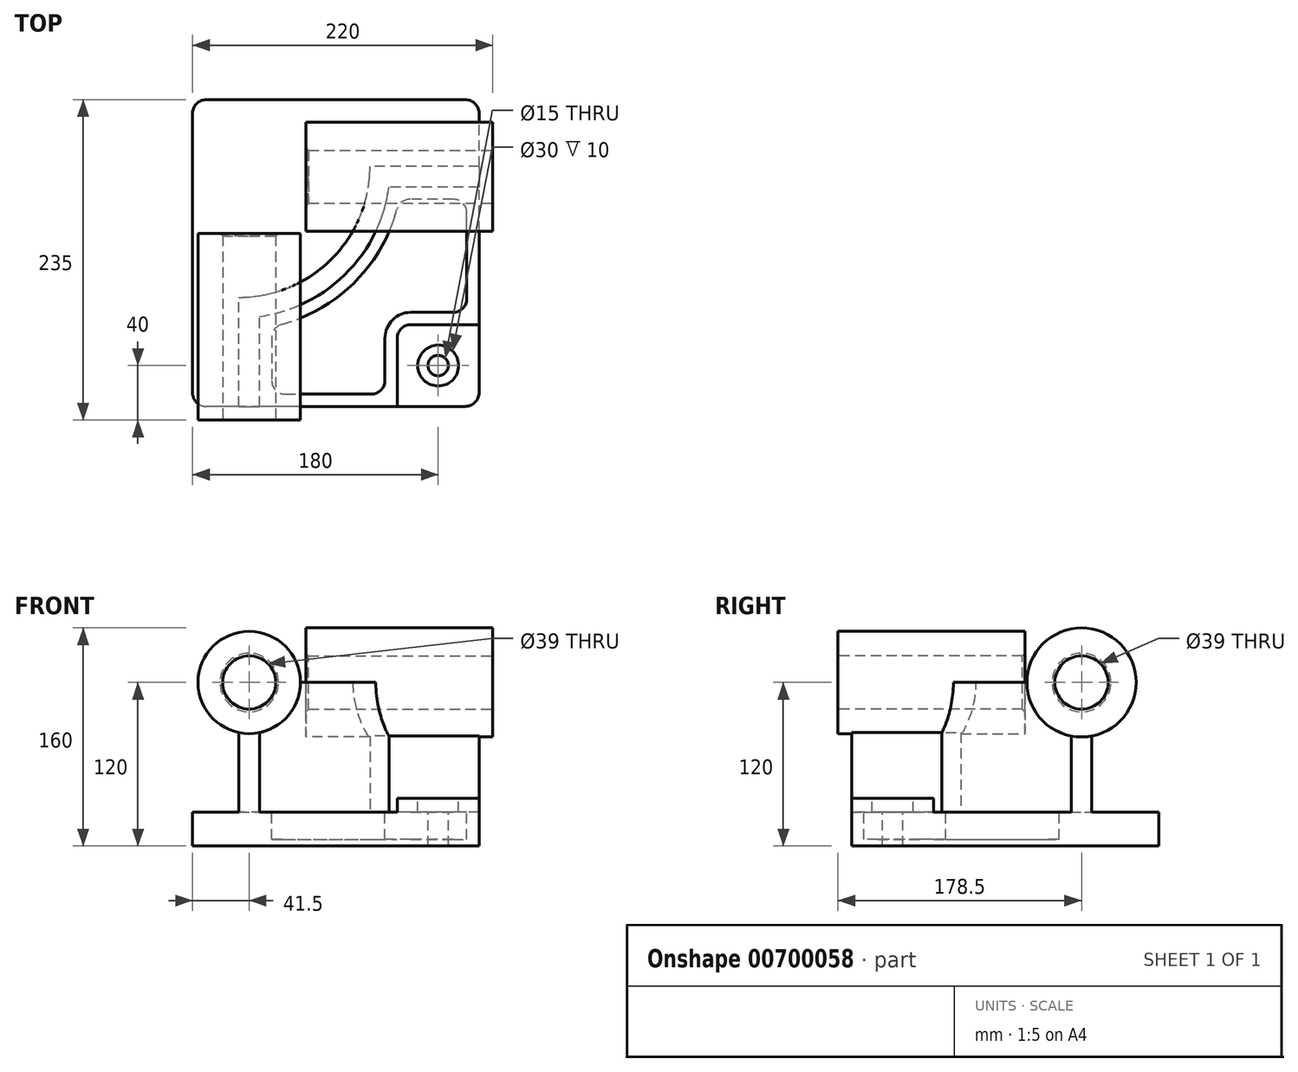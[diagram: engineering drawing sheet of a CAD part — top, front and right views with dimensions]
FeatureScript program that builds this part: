
annotation { "Feature Type Name" : "Feature", "Feature Type Description" : "" }
export const myFeature = defineFeature(function(context is Context, id is Id, definition is map)
    precondition{}
    {
        {
            var Q0;
            Q0=qCreatedBy(makeId("Top.planeOp"),FACE);
            var sketch = newSketch(context, id + "F0", { "sketchPlane" : qUnion([Q0])});
            skLineSegment(sketch, "E0.bottom", {"start": v(105, -112.5) * mm, "end": v(-105, -112.5) * mm});
            skLineSegment(sketch, "E0.top", {"start": v(105, 112.5) * mm, "end": v(-105, 112.5) * mm});
            skLineSegment(sketch, "E0.left", {"start": v(105, -112.5) * mm, "end": v(105, 112.5) * mm});
            skLineSegment(sketch, "E0.right", {"start": v(-105, -112.5) * mm, "end": v(-105, 112.5) * mm});
            skPoint(sketch, "E0.middle", {"position": v(0, 0) * mm});
            skSolve(sketch);
        }
        {
            var Q0;
            Q0=makeQuery(id+"F0.imprint","IMPRINT",FACE,{"disambiguationData":[TD([[makeQuery(id+"F0.imprint","IMPRINT",EDGE,{"derivedFrom":sQuery(id+"F0.wireOp",EDGE,"E0.bottom")}),-1.0]])]});
            extrude(context, id + "F1", {"entities" : qUnion([Q0]), "depth" : 25 * mm, "offsetDistance" : 25 * mm});
        }
        {
            var Q0;
            Q0=makeQuery(id+"F1.opExtrude","CAP_FACE",FACE,{"disambiguationData":[OSD([sQuery(id+"F0.wireOp",EDGE,"E0.bottom"),sQuery(id+"F0.wireOp",EDGE,"E0.top"),sQuery(id+"F0.wireOp",EDGE,"E0.left"),sQuery(id+"F0.wireOp",EDGE,"E0.right")])],"isStart":false});
            var sketch = newSketch(context, id + "F2", { "sketchPlane" : qUnion([Q0])});
            skLineSegment(sketch, "E1", {"start": v(-71, -112.5) * mm, "end": v(-71, -32.5) * mm});
            skLineSegment(sketch, "E2", {"start": v(105, 63.5) * mm, "end": v(25, 63.5) * mm});
            skArc(sketch, "E3", {"start": v(-71, -32.5) * mm, "mid": v(-3.12, -4.38) * mm, "end": v(25, 63.5) * mm});
            skLineSegment(sketch, "E4", {"start": v(-71, 63.5) * mm, "end": v(25, 63.5) * mm, "construction": true});
            skLineSegment(sketch, "E5", {"start": v(-71, 63.5) * mm, "end": v(-71, -32.5) * mm, "construction": true});
            skLineSegment(sketch, "E6.0", {"start": v(-56, -112.5) * mm, "end": v(-56, -46.48) * mm});
            skArc(sketch, "E6.1", {"start": v(-56, -46.48) * mm, "mid": v(7.49, -14.99) * mm, "end": v(38.98, 48.5) * mm});
            skLineSegment(sketch, "E6.2", {"start": v(105, 48.5) * mm, "end": v(38.98, 48.5) * mm});
            skLineSegment(sketch, "E7.0", {"start": v(105, -112.5) * mm, "end": v(105, 112.5) * mm});
            skLineSegment(sketch, "E8.0", {"start": v(105, -112.5) * mm, "end": v(-105, -112.5) * mm});
            skSolve(sketch);
        }
        {
            var Q0;
            {var subQ2=sQuery(id+"F2.wireOp",EDGE,"E1");Q0=makeQuery(id+"F2.imprint","IMPRINT",FACE,{"disambiguationData":[TD([[makeQuery(id+"F2.imprint","IMPRINT",EDGE,{"derivedFrom":subQ2}),-1.0]])]});}
            extrude(context, id + "F3", {"entities" : qUnion([Q0]), "operationType" : NewBodyOperationType.ADD, "depth" : 95 * mm, "offsetDistance" : 25 * mm});
        }
        {
            var Q0;
            Q0=makeQuery(id+"F3.boolean.opBoolean","MERGE",FACE,{"derivedFrom":[makeQuery(id+"F1.opExtrude","SWEPT_FACE",FACE,{"disambiguationData":[OSD([sQuery(id+"F0.wireOp",EDGE,"E0.bottom")])]}),makeQuery(id+"F3.opExtrude","SWEPT_FACE",FACE,{"disambiguationData":[OSD([sQuery(id+"F2.wireOp",EDGE,"E8.0")])]})]});
            var sketch = newSketch(context, id + "F4", { "sketchPlane" : qUnion([Q0])});
            skCircle(sketch, "E9", {"center": v(-63.5, 120) * mm, "radius": 37.5 * mm});
            skSolve(sketch);
        }
        {
            var Q0;
            Q0 = qSketchRegion(id + "F4", true);
            extrude(context, id + "F5", {"entities" : qUnion([Q0]), "operationType" : NewBodyOperationType.ADD, "depth" : 10 * mm, "offsetDistance" : 25 * mm, "hasSecondDirection" : true, "secondDirectionOppositeDirection" : true, "secondDirectionDepth" : (137 - 10) * mm});
        }
        {
            var Q0;
            Q0=makeQuery(id+"F3.boolean.opBoolean","MERGE",FACE,{"derivedFrom":[makeQuery(id+"F1.opExtrude","SWEPT_FACE",FACE,{"disambiguationData":[OSD([sQuery(id+"F0.wireOp",EDGE,"E0.left")])]}),makeQuery(id+"F3.opExtrude","SWEPT_FACE",FACE,{"disambiguationData":[OSD([sQuery(id+"F2.wireOp",EDGE,"E7.0")])]})]});
            var sketch = newSketch(context, id + "F6", { "sketchPlane" : qUnion([Q0])});
            skCircle(sketch, "E10", {"center": v(56, 120) * mm, "radius": 40 * mm});
            skSolve(sketch);
        }
        {
            var Q0;
            Q0 = qSketchRegion(id + "F6", true);
            extrude(context, id + "F7", {"entities" : qUnion([Q0]), "operationType" : NewBodyOperationType.ADD, "depth" : 10 * mm, "offsetDistance" : 25 * mm, "hasSecondDirection" : true, "secondDirectionOppositeDirection" : true, "secondDirectionDepth" : (137 - 10) * mm});
        }
        {
            var Q0;
            {var subQ0=sQuery(id+"F0.wireOp",EDGE,"E0.left");var subQ1=sQuery(id+"F0.wireOp",EDGE,"E0.bottom");Q0=makeQuery(id+"F3.boolean.opBoolean","SPLIT",FACE,{"disambiguationData":[TD([makeQuery(id+"F3.opExtrude","SWEPT_FACE",FACE,{"disambiguationData":[OSD([sQuery(id+"F2.wireOp",EDGE,"E6.0")])]})])],"derivedFrom":makeQuery(id+"F1.opExtrude","CAP_FACE",FACE,{"disambiguationData":[OSD([subQ1,sQuery(id+"F0.wireOp",EDGE,"E0.top"),subQ0,sQuery(id+"F0.wireOp",EDGE,"E0.right")])],"isStart":false})});}
            var sketch = newSketch(context, id + "F8", { "sketchPlane" : qUnion([Q0])});
            skLineSegment(sketch, "E11.bottom", {"start": v(105, -112.5) * mm, "end": v(45, -112.5) * mm});
            skLineSegment(sketch, "E11.top", {"start": v(105, -52.5) * mm, "end": v(45, -52.5) * mm});
            skLineSegment(sketch, "E11.left", {"start": v(105, -112.5) * mm, "end": v(105, -52.5) * mm});
            skLineSegment(sketch, "E11.right", {"start": v(45, -112.5) * mm, "end": v(45, -52.5) * mm});
            skSolve(sketch);
        }
        {
            var Q0;
            Q0 = qSketchRegion(id + "F8", true);
            extrude(context, id + "F9", {"entities" : qUnion([Q0]), "operationType" : NewBodyOperationType.ADD, "depth" : (35 - 25) * mm, "offsetDistance" : 25 * mm});
        }
        {
            var Q0;
            Q0=makeQuery(id+"F9.opExtrude","SWEPT_EDGE",EDGE,{"disambiguationData":[OSD([sQuery(id+"F8.wireOp",EDGE,"E11.top"),sQuery(id+"F8.wireOp",EDGE,"E11.right")])]});
            fillet(context, id + "F10", {"entities" : qUnion([Q0]), "radius" : 10 * mm, "tangentPropagation" : true, "allowEdgeOverflow" : false});
        }
        {
            var Q0;
            {var subQ0=sQuery(id+"F0.wireOp",EDGE,"E0.left");var subQ1=sQuery(id+"F0.wireOp",EDGE,"E0.bottom");Q0=makeQuery(id+"F3.boolean.opBoolean","SPLIT",FACE,{"disambiguationData":[TD([makeQuery(id+"F3.opExtrude","SWEPT_FACE",FACE,{"disambiguationData":[OSD([sQuery(id+"F2.wireOp",EDGE,"E6.0")])]})])],"derivedFrom":makeQuery(id+"F1.opExtrude","CAP_FACE",FACE,{"disambiguationData":[OSD([subQ1,sQuery(id+"F0.wireOp",EDGE,"E0.top"),subQ0,sQuery(id+"F0.wireOp",EDGE,"E0.right")])],"isStart":false})});}
            var sketch = newSketch(context, id + "F11", { "sketchPlane" : qUnion([Q0])});
            skLineSegment(sketch, "E12.0", {"start": v(-47, -54.08) * mm, "end": v(-47, -103.5) * mm});
            skArc(sketch, "E12.1", {"start": v(46.58, 39.5) * mm, "mid": v(13.85, -21.35) * mm, "end": v(-47, -54.08) * mm});
            skLineSegment(sketch, "E12.2", {"start": v(-47, -103.5) * mm, "end": v(36, -103.5) * mm});
            skLineSegment(sketch, "E12.3", {"start": v(96, 39.5) * mm, "end": v(46.58, 39.5) * mm});
            skLineSegment(sketch, "E12.4", {"start": v(36, -103.5) * mm, "end": v(36, -62.5) * mm});
            skArc(sketch, "E12.5", {"start": v(36, -62.5) * mm, "mid": v(41.56, -49.06) * mm, "end": v(55, -43.5) * mm});
            skLineSegment(sketch, "E12.6", {"start": v(55, -43.5) * mm, "end": v(96, -43.5) * mm});
            skLineSegment(sketch, "E12.7", {"start": v(96, -43.5) * mm, "end": v(96, 39.5) * mm});
            skSolve(sketch);
        }
        {
            var Q0;
            Q0=makeQuery(id+"F11.imprint","IMPRINT",FACE,{"disambiguationData":[TD([[makeQuery(id+"F11.imprint","IMPRINT",EDGE,{"derivedFrom":sQuery(id+"F11.wireOp",EDGE,"E12.0")}),1.0]])]});
            extrude(context, id + "F12", {"entities" : qUnion([Q0]), "operationType" : NewBodyOperationType.REMOVE, "oppositeDirection" : true, "depth" : (25 - 5) * mm, "offsetDistance" : 25 * mm});
        }
        {
            var Q0;
            Q0=makeQuery(id+"F9.opExtrude","CAP_FACE",FACE,{"disambiguationData":[OSD([sQuery(id+"F8.wireOp",EDGE,"E11.bottom"),sQuery(id+"F8.wireOp",EDGE,"E11.top"),sQuery(id+"F8.wireOp",EDGE,"E11.left"),sQuery(id+"F8.wireOp",EDGE,"E11.right")])],"isStart":false});
            var sketch = newSketch(context, id + "F13", { "sketchPlane" : qUnion([Q0])});
            skCircle(sketch, "E13", {"center": v(75, -82.5) * mm, "radius": 15 * mm});
            skPoint(sketch, "E13.centerSnap0", {"position": v(75, -112.5) * mm});
            skPoint(sketch, "E13.centerSnap1", {"position": v(105, -82.5) * mm});
            skSolve(sketch);
        }
        {
            var Q0;
            Q0=sQuery(id+"F13.wireOp",VERTEX,"E13.center");
            var Q1;
            Q1=makeQuery(id+"F1.opExtrude","SWEPT_BODY",BODY,{"disambiguationData":[OSD([sQuery(id+"F0.wireOp",EDGE,"E0.bottom"),sQuery(id+"F0.wireOp",EDGE,"E0.top"),sQuery(id+"F0.wireOp",EDGE,"E0.left"),sQuery(id+"F0.wireOp",EDGE,"E0.right")])]});
            hole(context, id + "F14", {"style" : HoleStyle.C_BORE, "endStyle" : HoleEndStyle.THROUGH, "holeDiameter" : 15 * mm, "cBoreDiameter" : 30 * mm, "cBoreDepth" : 10 * mm, "majorDiameter" : 5 * mm, "isTappedThrough" : true, "tappedDepth" : 12 * mm, "tapClearance" : 3, "locations" : qUnion([Q0]), "scope" : qUnion([Q1])});
        }
        {
            var Q0;
            Q0=makeQuery(id+"F12.boolean.opBoolean","COPY",EDGE,{"derivedFrom":makeQuery(id+"F12.opExtrude","SWEPT_EDGE",EDGE,{"disambiguationData":[OSD([sQuery(id+"F11.wireOp",EDGE,"E12.0"),sQuery(id+"F11.wireOp",EDGE,"E12.1")])]})});
            var Q1;
            Q1=makeQuery(id+"F12.boolean.opBoolean","COPY",EDGE,{"derivedFrom":makeQuery(id+"F12.opExtrude","SWEPT_EDGE",EDGE,{"disambiguationData":[OSD([sQuery(id+"F11.wireOp",EDGE,"E12.1"),sQuery(id+"F11.wireOp",EDGE,"E12.3")])]})});
            var Q2;
            Q2=makeQuery(id+"F12.boolean.opBoolean","COPY",EDGE,{"derivedFrom":makeQuery(id+"F12.opExtrude","SWEPT_EDGE",EDGE,{"disambiguationData":[OSD([sQuery(id+"F11.wireOp",EDGE,"E12.3"),sQuery(id+"F11.wireOp",EDGE,"E12.7")])]})});
            var Q3;
            Q3=makeQuery(id+"F12.boolean.opBoolean","COPY",EDGE,{"derivedFrom":makeQuery(id+"F12.opExtrude","SWEPT_EDGE",EDGE,{"disambiguationData":[OSD([sQuery(id+"F11.wireOp",EDGE,"E12.6"),sQuery(id+"F11.wireOp",EDGE,"E12.7")])]})});
            var Q4;
            Q4=makeQuery(id+"F12.boolean.opBoolean","COPY",EDGE,{"derivedFrom":makeQuery(id+"F12.opExtrude","SWEPT_EDGE",EDGE,{"disambiguationData":[OSD([sQuery(id+"F11.wireOp",EDGE,"E12.2"),sQuery(id+"F11.wireOp",EDGE,"E12.4")])]})});
            var Q5;
            Q5=makeQuery(id+"F12.boolean.opBoolean","COPY",EDGE,{"derivedFrom":makeQuery(id+"F12.opExtrude","SWEPT_EDGE",EDGE,{"disambiguationData":[OSD([sQuery(id+"F11.wireOp",EDGE,"E12.0"),sQuery(id+"F11.wireOp",EDGE,"E12.2")])]})});
            fillet(context, id + "F15", {"entities" : qUnion([Q0, Q1, Q2, Q3, Q4, Q5]), "radius" : 10 * mm, "tangentPropagation" : true, "allowEdgeOverflow" : false});
        }
        {
            var Q0;
            Q0=makeQuery(id+"F5.opExtrude","CAP_FACE",FACE,{"disambiguationData":[OSD([sQuery(id+"F4.wireOp",EDGE,"E9")])],"isStart":false});
            var sketch = newSketch(context, id + "F16", { "sketchPlane" : qUnion([Q0])});
            skCircle(sketch, "E14", {"center": v(-63.5, 120) * mm, "radius": 19.5 * mm});
            skSolve(sketch);
        }
        {
            var Q0;
            Q0 = qSketchRegion(id + "F16", true);
            extrude(context, id + "F17", {"entities" : qUnion([Q0]), "operationType" : NewBodyOperationType.REMOVE, "endBound" : BoundingType.THROUGH_ALL, "oppositeDirection" : true, "depth" : 25 * mm, "offsetDistance" : 25 * mm});
        }
        {
            var Q0;
            Q0=makeQuery(id+"F7.opExtrude","CAP_FACE",FACE,{"disambiguationData":[OSD([sQuery(id+"F6.wireOp",EDGE,"E10")])],"isStart":false});
            var sketch = newSketch(context, id + "F18", { "sketchPlane" : qUnion([Q0])});
            skCircle(sketch, "E15", {"center": v(56, 120) * mm, "radius": 19.5 * mm});
            skSolve(sketch);
        }
        {
            var Q0;
            Q0 = qSketchRegion(id + "F18", true);
            extrude(context, id + "F19", {"entities" : qUnion([Q0]), "operationType" : NewBodyOperationType.REMOVE, "endBound" : BoundingType.THROUGH_ALL, "oppositeDirection" : true, "depth" : 25 * mm, "offsetDistance" : 25 * mm});
        }
        {
            var Q0;
            Q0=makeQuery(id+"F17.boolean.opBoolean","COPY",EDGE,{"derivedFrom":makeQuery(id+"F17.opExtrude","CAP_EDGE",EDGE,{"disambiguationData":[OSD([sQuery(id+"F16.wireOp",EDGE,"E14")])],"isStart":true})});
            var Q1;
            Q1=makeQuery(id+"F19.boolean.opBoolean","COPY",EDGE,{"derivedFrom":makeQuery(id+"F19.opExtrude","CAP_EDGE",EDGE,{"disambiguationData":[OSD([sQuery(id+"F18.wireOp",EDGE,"E15")])],"isStart":true})});
            var Q2;
            Q2=makeQuery(id+"F17.boolean.opBoolean","INTERSECT",EDGE,{"derivedFrom":[makeQuery(id+"F5.opExtrude","CAP_FACE",FACE,{"disambiguationData":[OSD([sQuery(id+"F4.wireOp",EDGE,"E9")])],"isStart":true}),makeQuery(id+"F17.opExtrude","SWEPT_FACE",FACE,{"disambiguationData":[OSD([sQuery(id+"F16.wireOp",EDGE,"E14")])]})]});
            var Q3;
            Q3=makeQuery(id+"F19.boolean.opBoolean","INTERSECT",EDGE,{"derivedFrom":[makeQuery(id+"F7.opExtrude","CAP_FACE",FACE,{"disambiguationData":[OSD([sQuery(id+"F6.wireOp",EDGE,"E10")])],"isStart":true}),makeQuery(id+"F19.opExtrude","SWEPT_FACE",FACE,{"disambiguationData":[OSD([sQuery(id+"F18.wireOp",EDGE,"E15")])]})]});
            chamfer(context, id + "F20", {"entities" : qUnion([Q0, Q1, Q2, Q3]), "width" : 2 * mm, "tangentPropagation" : true});
        }
        {
            var Q0;
            Q0=makeQuery(id+"F9.boolean.opBoolean","MERGE",EDGE,{"derivedFrom":[makeQuery(id+"F1.opExtrude","SWEPT_EDGE",EDGE,{"disambiguationData":[OSD([sQuery(id+"F0.wireOp",EDGE,"E0.bottom"),sQuery(id+"F0.wireOp",EDGE,"E0.left")])]}),makeQuery(id+"F9.opExtrude","SWEPT_EDGE",EDGE,{"disambiguationData":[OSD([sQuery(id+"F8.wireOp",EDGE,"E11.bottom"),sQuery(id+"F8.wireOp",EDGE,"E11.left")])]})]});
            var Q1;
            Q1=makeQuery(id+"F1.opExtrude","SWEPT_EDGE",EDGE,{"disambiguationData":[OSD([sQuery(id+"F0.wireOp",EDGE,"E0.top"),sQuery(id+"F0.wireOp",EDGE,"E0.left")])]});
            var Q2;
            Q2=makeQuery(id+"F1.opExtrude","SWEPT_EDGE",EDGE,{"disambiguationData":[OSD([sQuery(id+"F0.wireOp",EDGE,"E0.top"),sQuery(id+"F0.wireOp",EDGE,"E0.right")])]});
            var Q3;
            Q3=makeQuery(id+"F1.opExtrude","SWEPT_EDGE",EDGE,{"disambiguationData":[OSD([sQuery(id+"F0.wireOp",EDGE,"E0.bottom"),sQuery(id+"F0.wireOp",EDGE,"E0.right")])]});
            fillet(context, id + "F21", {"entities" : qUnion([Q0, Q1, Q2, Q3]), "radius" : 10 * mm, "tangentPropagation" : true, "allowEdgeOverflow" : false});
        }
    });
